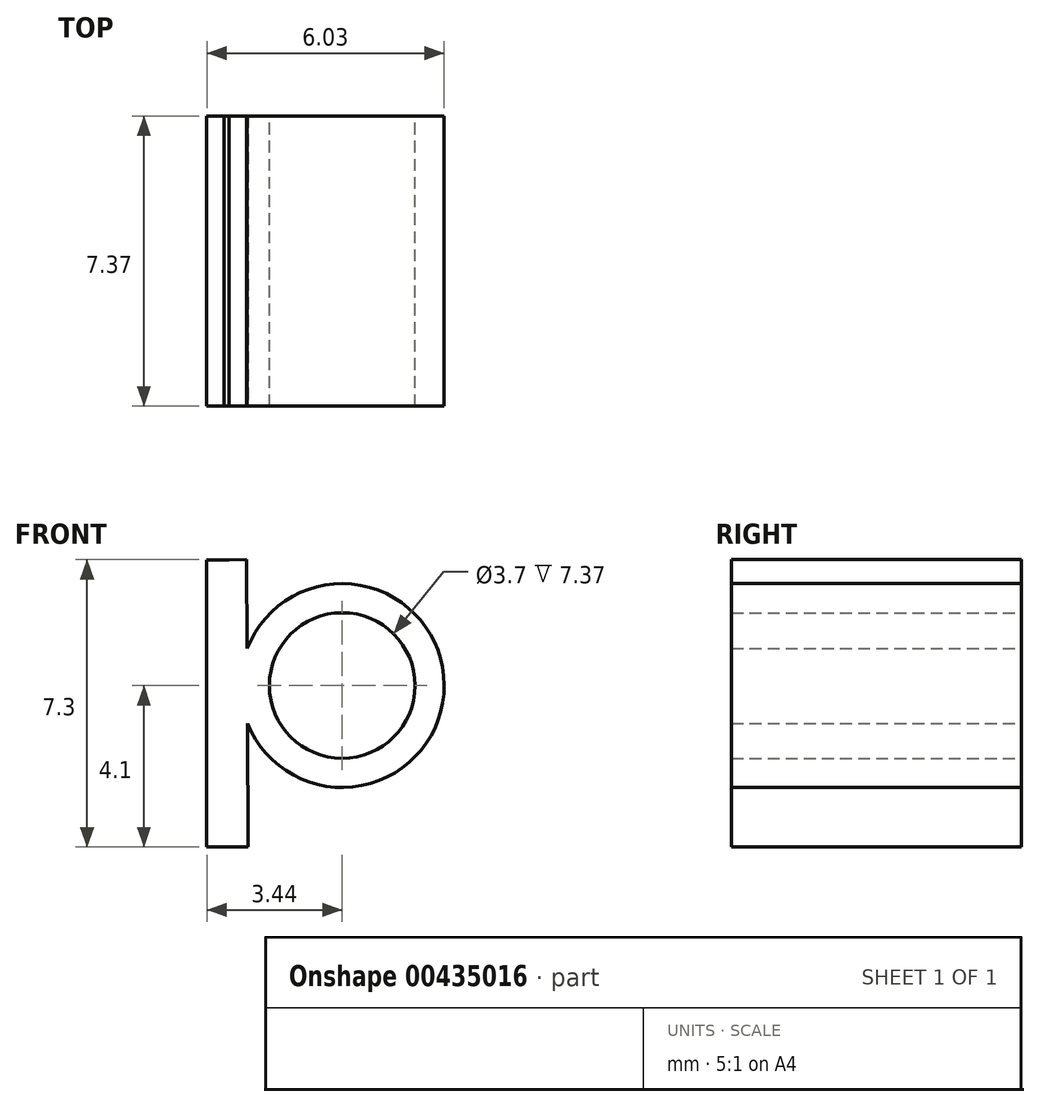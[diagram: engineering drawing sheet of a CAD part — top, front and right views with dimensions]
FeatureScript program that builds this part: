
annotation { "Feature Type Name" : "Feature", "Feature Type Description" : "" }
export const myFeature = defineFeature(function(context is Context, id is Id, definition is map)
    precondition{}
    {
        {
            var Q0;
            Q0=qCreatedBy(makeId("Front.planeOp"),FACE);
            var sketch = newSketch(context, id + "F0", { "sketchPlane" : qUnion([Q0])});
            skCircle(sketch, "E0", {"center": v(0, 0) * mm, "radius": 2.6 * mm});
            skCircle(sketch, "E1", {"center": v(0, 0) * mm, "radius": 1.85 * mm});
            skSolve(sketch);
        }
        {
            var Q0;
            Q0 = qSketchRegion(id + "F0", true);
            extrude(context, id + "F1", {"entities" : qUnion([Q0]), "depth" : 7.37 * mm, "offsetDistance" : 25 * mm});
        }
        {
            var Q0;
            Q0=makeQuery(id+"F1.opExtrude","CAP_FACE",FACE,{"disambiguationData":[OSD([sQuery(id+"F0.wireOp",EDGE,"E0"),sQuery(id+"F0.wireOp",EDGE,"E1")])],"isStart":false});
            var sketch = newSketch(context, id + "F2", { "sketchPlane" : qUnion([Q0])});
            skLineSegment(sketch, "E2", {"start": v(-3.44, 4.27) * mm, "end": v(-3.44, -4.1) * mm});
            skLineSegment(sketch, "E3", {"start": v(-3.44, -4.1) * mm, "end": v(-2.4, -4.1) * mm});
            skLineSegment(sketch, "E4", {"start": v(-3.44, 4.27) * mm, "end": v(-2.43, 4.27) * mm});
            skLineSegment(sketch, "E5", {"start": v(-2.43, 4.27) * mm, "end": v(-2.4, -4.1) * mm});
            skSolve(sketch);
        }
        {
            var Q0;
            Q0 = qSketchRegion(id + "F2", true);
            extrude(context, id + "F3", {"entities" : qUnion([Q0]), "operationType" : NewBodyOperationType.ADD, "oppositeDirection" : true, "depth" : 7.37 * mm, "offsetDistance" : 25 * mm});
        }
        {
            var Q0;
            Q0=makeQuery(id+"F3.boolean.opBoolean","MERGE",FACE,{"derivedFrom":[makeQuery(id+"F1.opExtrude","CAP_FACE",FACE,{"disambiguationData":[OSD([sQuery(id+"F0.wireOp",EDGE,"E0"),sQuery(id+"F0.wireOp",EDGE,"E1")])],"isStart":false}),makeQuery(id+"F3.opExtrude","CAP_FACE",FACE,{"disambiguationData":[OSD([sQuery(id+"F2.wireOp",EDGE,"E2"),sQuery(id+"F2.wireOp",EDGE,"E3"),sQuery(id+"F2.wireOp",EDGE,"E4"),sQuery(id+"F2.wireOp",EDGE,"E5")])],"isStart":true})]});
            var sketch = newSketch(context, id + "F4", { "sketchPlane" : qUnion([Q0])});
            skCircle(sketch, "E6", {"center": v(-2.94, 3.45) * mm, "radius": 0.27 * mm});
            skSolve(sketch);
        }
        {
            var Q0;
            Q0 = qSketchRegion(id + "F4", true);
            extrude(context, id + "F5", {"entities" : qUnion([Q0]), "operationType" : NewBodyOperationType.REMOVE, "oppositeDirection" : true, "depth" : 25 * mm, "offsetDistance" : 25 * mm});
        }
        {
            var Q0;
            Q0=makeQuery(id+"F3.boolean.opBoolean","MERGE",FACE,{"derivedFrom":[makeQuery(id+"F1.opExtrude","CAP_FACE",FACE,{"disambiguationData":[OSD([sQuery(id+"F0.wireOp",EDGE,"E0"),sQuery(id+"F0.wireOp",EDGE,"E1")])],"isStart":false}),makeQuery(id+"F3.opExtrude","CAP_FACE",FACE,{"disambiguationData":[OSD([sQuery(id+"F2.wireOp",EDGE,"E2"),sQuery(id+"F2.wireOp",EDGE,"E3"),sQuery(id+"F2.wireOp",EDGE,"E4"),sQuery(id+"F2.wireOp",EDGE,"E5")])],"isStart":true})]});
            var sketch = newSketch(context, id + "F6", { "sketchPlane" : qUnion([Q0])});
            skLineSegment(sketch, "E7", {"start": v(-2.94, 3.19) * mm, "end": v(-2.42, 3.2) * mm});
            skLineSegment(sketch, "E8", {"start": v(-2.42, 3.2) * mm, "end": v(-3.44, 3.19) * mm});
            skLineSegment(sketch, "E9", {"start": v(-3.44, 3.19) * mm, "end": v(-4.5, 4.55) * mm});
            skLineSegment(sketch, "E10", {"start": v(-4.5, 4.55) * mm, "end": v(-2.57, 4.8) * mm});
            skLineSegment(sketch, "E11", {"start": v(-2.57, 4.8) * mm, "end": v(-1.58, 4) * mm});
            skLineSegment(sketch, "E12", {"start": v(-1.58, 4) * mm, "end": v(-2.42, 3.2) * mm});
            skSolve(sketch);
        }
        {
            var Q0;
            Q0 = qSketchRegion(id + "F6", true);
            extrude(context, id + "F7", {"entities" : qUnion([Q0]), "operationType" : NewBodyOperationType.REMOVE, "oppositeDirection" : true, "depth" : 25 * mm, "offsetDistance" : 25 * mm});
        }
    });
